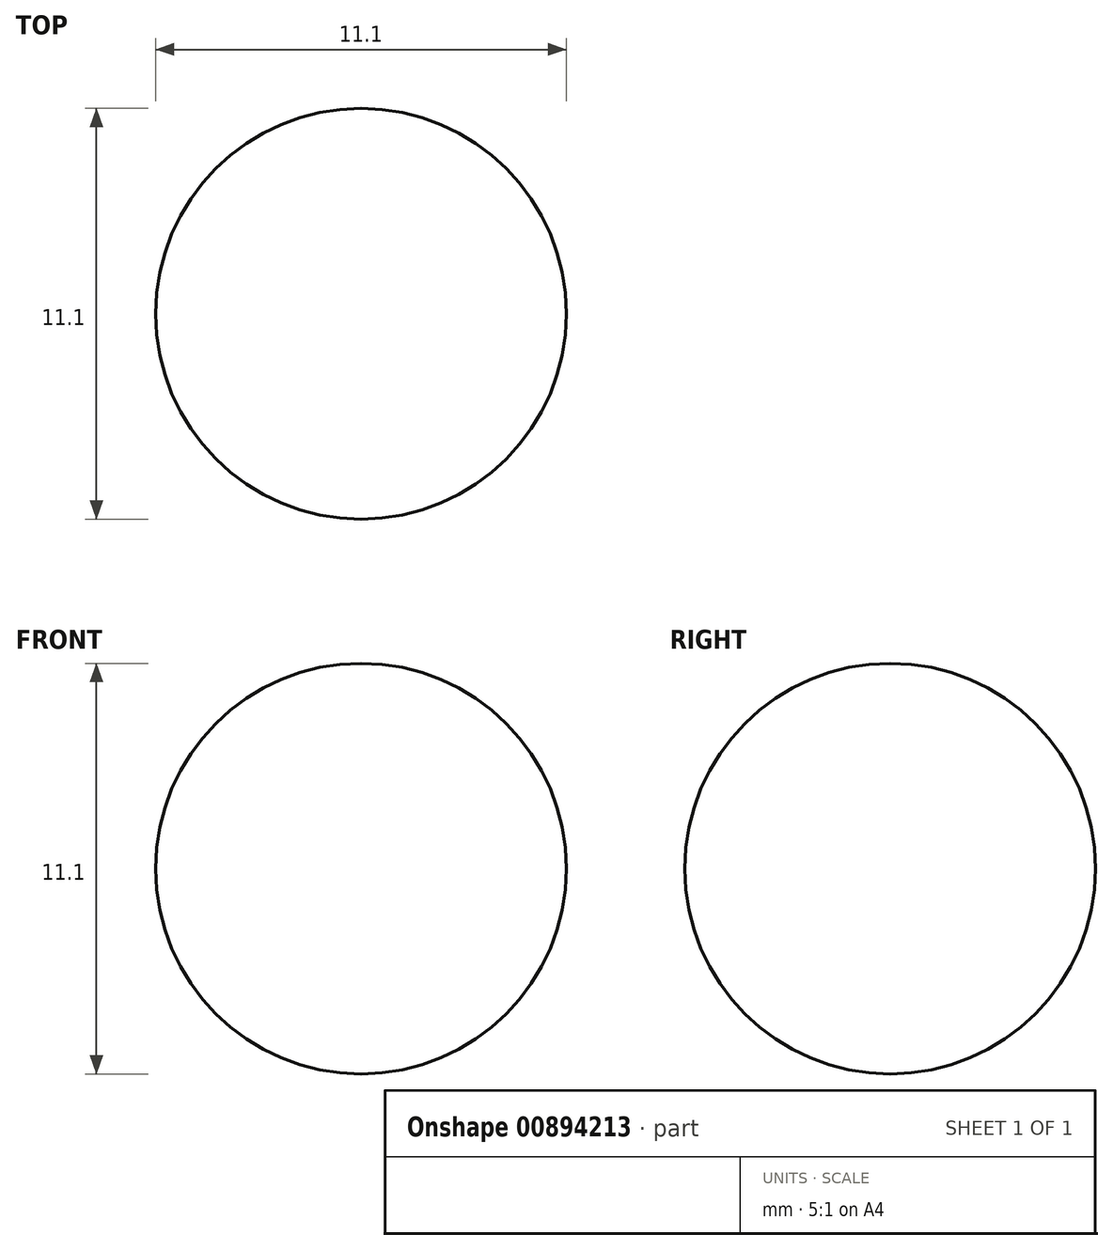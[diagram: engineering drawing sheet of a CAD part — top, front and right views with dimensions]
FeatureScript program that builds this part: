
annotation { "Feature Type Name" : "Feature", "Feature Type Description" : "" }
export const myFeature = defineFeature(function(context is Context, id is Id, definition is map)
    precondition{}
    {
        {
            var Q0;
            Q0=qCreatedBy(makeId("Front.planeOp"),FACE);
            var sketch = newSketch(context, id + "F0", { "sketchPlane" : qUnion([Q0])});
            skLineSegment(sketch, "E0", {"start": v(0, 5.55) * mm, "end": v(0, -5.55) * mm});
            skArc(sketch, "E1", {"start": v(0, -5.55) * mm, "mid": v(5.55, 0) * mm, "end": v(0, 5.55) * mm});
            skSolve(sketch);
        }
        {
            var Q0;
            Q0=makeQuery(id+"F0.imprint","IMPRINT",FACE,{"disambiguationData":[TD([[makeQuery(id+"F0.imprint","IMPRINT",EDGE,{"derivedFrom":sQuery(id+"F0.wireOp",EDGE,"E0")}),1.0]])]});
            var Q1;
            Q1=sQuery(id+"F0.wireOp",EDGE,"E0");
            revolve(context, id + "F1", {"surfaceOperationType" : NewSurfaceOperationType.NEW, "entities" : qUnion([Q0]), "axis" : qUnion([Q1]), "revolveType" : RevolveType.FULL});
        }
    });
